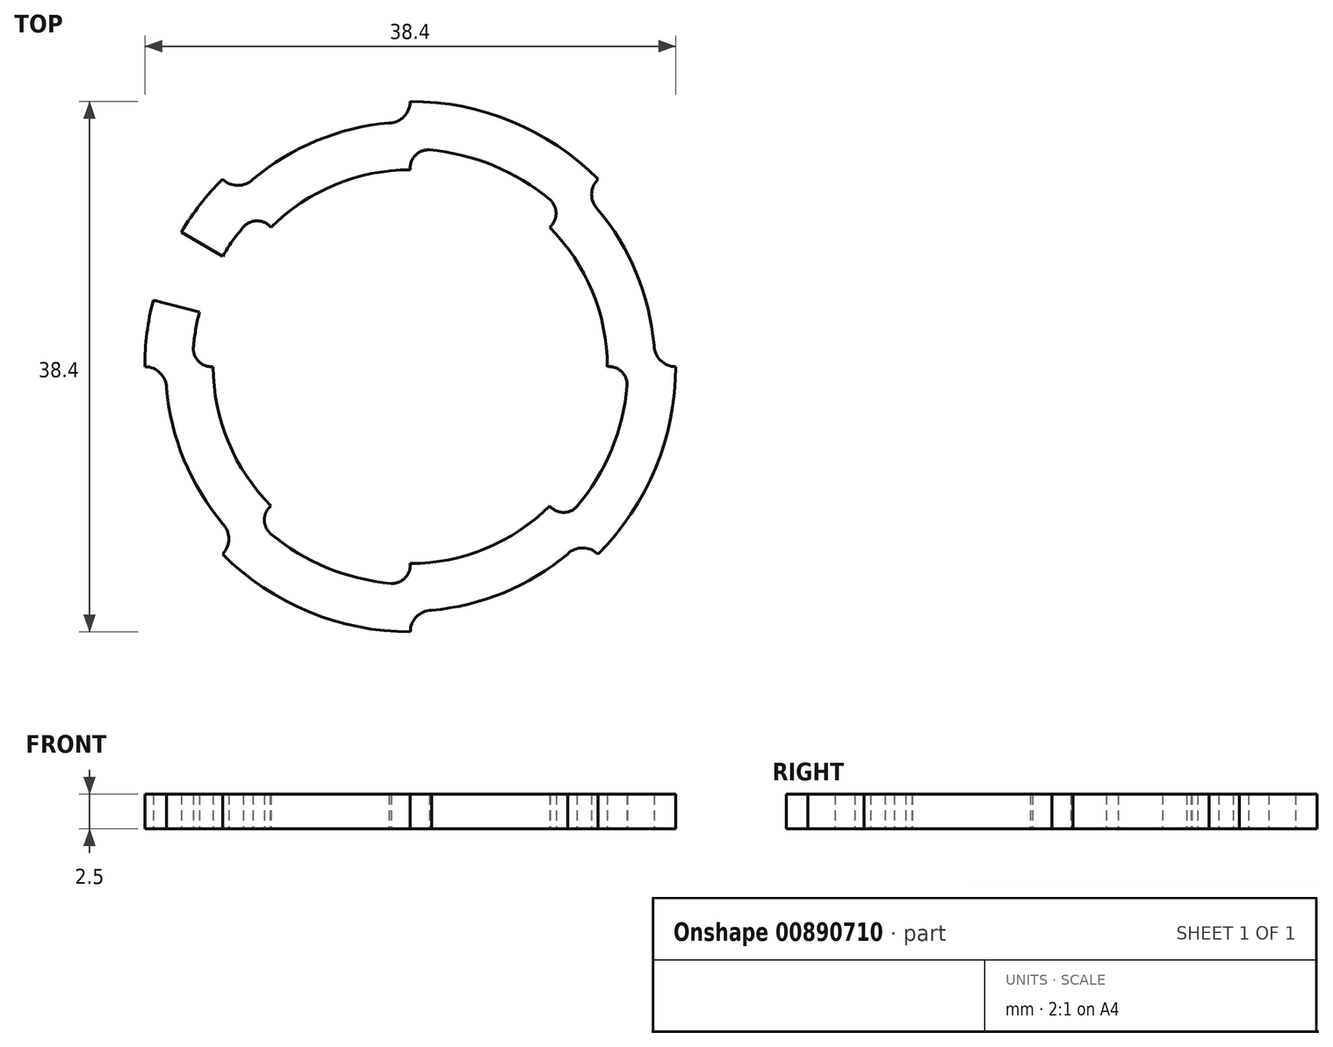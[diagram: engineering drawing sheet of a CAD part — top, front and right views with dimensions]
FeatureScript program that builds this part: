
annotation { "Feature Type Name" : "Feature", "Feature Type Description" : "" }
export const myFeature = defineFeature(function(context is Context, id is Id, definition is map)
    precondition{}
    {
        {
            var Q0;
            Q0=qCreatedBy(makeId("Top.planeOp"),FACE);
            var sketch = newSketch(context, id + "F0", { "sketchPlane" : qUnion([Q0])});
            skCircle(sketch, "E0", {"center": v(0, 0) * mm, "radius": 19.2 * mm, "construction": true});
            skArc(sketch, "E1", {"start": v(-13.58, 13.58) * mm, "mid": v(-17.74, 7.35) * mm, "end": v(-19.2, 0) * mm});
            skArc(sketch, "E2.1.0", {"start": v(13.58, 13.58) * mm, "mid": v(7.35, 17.74) * mm, "end": v(0, 19.2) * mm});
            skArc(sketch, "E2.2.0", {"start": v(13.58, -13.58) * mm, "mid": v(17.74, -7.35) * mm, "end": v(19.2, 0) * mm});
            skArc(sketch, "E2.3.0", {"start": v(-13.58, -13.58) * mm, "mid": v(-7.35, -17.74) * mm, "end": v(0, -19.2) * mm});
            skLineSegment(sketch, "E2.anchor1", {"start": v(0, 0) * mm, "end": v(-19.2, 0) * mm, "construction": true});
            skLineSegment(sketch, "E2.anchor2", {"start": v(0, 0) * mm, "end": v(0, -19.2) * mm, "construction": true});
            skCircle(sketch, "E3", {"center": v(0, 0) * mm, "radius": 17.7 * mm, "construction": true});
            skLineSegment(sketch, "E4", {"start": v(0, 0) * mm, "end": v(13.58, -13.58) * mm, "construction": true});
            skLineSegment(sketch, "E5", {"start": v(0, 0) * mm, "end": v(14.28, -17.02) * mm, "construction": true});
            skLineSegment(sketch, "E6", {"start": v(0, 0) * mm, "end": v(20.43, 1.79) * mm, "construction": true});
            skLineSegment(sketch, "E7", {"start": v(0, 0) * mm, "end": v(1.79, -20.44) * mm, "construction": true});
            skPoint(sketch, "E8", {"position": v(11.38, -13.56) * mm});
            skPoint(sketch, "E9", {"position": v(1.54, -17.63) * mm});
            skPoint(sketch, "E10", {"position": v(17.63, 1.54) * mm});
            skArc(sketch, "E11", {"start": v(13.58, -13.58) * mm, "mid": v(12.48, -13.12) * mm, "end": v(11.38, -13.56) * mm});
            skArc(sketch, "E12", {"start": v(1.54, -17.63) * mm, "mid": v(0.45, -18.1) * mm, "end": v(0, -19.2) * mm});
            skLineSegment(sketch, "E13", {"start": v(0, 0) * mm, "end": v(-20.95, -1.83) * mm, "construction": true});
            skLineSegment(sketch, "E14", {"start": v(0, 0) * mm, "end": v(-13.58, -13.58) * mm, "construction": true});
            skLineSegment(sketch, "E15", {"start": v(0, 0) * mm, "end": v(-18.25, -15.32) * mm, "construction": true});
            skArc(sketch, "E16", {"start": v(17.63, 1.54) * mm, "mid": v(18.1, 0.45) * mm, "end": v(19.2, 0) * mm});
            skArc(sketch, "E17", {"start": v(11.38, -13.56) * mm, "mid": v(6.77, -16.35) * mm, "end": v(1.54, -17.63) * mm});
            skArc(sketch, "E18", {"start": v(-13.56, -11.38) * mm, "mid": v(-16.35, -6.77) * mm, "end": v(-17.63, -1.54) * mm});
            skArc(sketch, "E19", {"start": v(-13.58, -13.58) * mm, "mid": v(-13.12, -12.48) * mm, "end": v(-13.56, -11.38) * mm});
            skArc(sketch, "E20", {"start": v(-17.63, -1.54) * mm, "mid": v(-18.1, -0.45) * mm, "end": v(-19.2, 0) * mm});
            skLineSegment(sketch, "E21", {"start": v(0, 0) * mm, "end": v(-13.58, 13.58) * mm, "construction": true});
            skLineSegment(sketch, "E22", {"start": v(0, 0) * mm, "end": v(-14.48, 17.25) * mm, "construction": true});
            skLineSegment(sketch, "E23", {"start": v(0, 0) * mm, "end": v(-1.93, 22.01) * mm, "construction": true});
            skLineSegment(sketch, "E24", {"start": v(0, 0) * mm, "end": v(13.58, 13.58) * mm, "construction": true});
            skLineSegment(sketch, "E25", {"start": v(0, 0) * mm, "end": v(16.66, 13.98) * mm, "construction": true});
            skArc(sketch, "E26", {"start": v(-11.38, 13.56) * mm, "mid": v(-6.77, 16.35) * mm, "end": v(-1.54, 17.63) * mm});
            skArc(sketch, "E27", {"start": v(13.56, 11.38) * mm, "mid": v(16.35, 6.77) * mm, "end": v(17.63, 1.54) * mm});
            skArc(sketch, "E28", {"start": v(-13.58, 13.58) * mm, "mid": v(-12.48, 13.12) * mm, "end": v(-11.38, 13.56) * mm});
            skArc(sketch, "E29", {"start": v(-1.54, 17.63) * mm, "mid": v(-0.45, 18.1) * mm, "end": v(0, 19.2) * mm});
            skArc(sketch, "E30", {"start": v(13.58, 13.58) * mm, "mid": v(13.12, 12.48) * mm, "end": v(13.56, 11.38) * mm});
            skLineSegment(sketch, "E31", {"start": v(0, 0) * mm, "end": v(17.2, -14.44) * mm, "construction": true});
            skLineSegment(sketch, "E32", {"start": v(0, 0) * mm, "end": v(23.4, -2.05) * mm, "construction": true});
            skArc(sketch, "E33", {"start": v(12.07, -10.12) * mm, "mid": v(14.55, -6.03) * mm, "end": v(15.7, -1.37) * mm});
            skLineSegment(sketch, "E34", {"start": v(0, 0) * mm, "end": v(-1.9, -21.71) * mm, "construction": true});
            skLineSegment(sketch, "E35", {"start": v(0, 0) * mm, "end": v(-14, -16.68) * mm, "construction": true});
            skArc(sketch, "E36", {"start": v(-1.37, -15.7) * mm, "mid": v(-6.03, -14.55) * mm, "end": v(-10.12, -12.07) * mm});
            skLineSegment(sketch, "E37", {"start": v(0, 0) * mm, "end": v(-21.5, 1.88) * mm, "construction": true});
            skLineSegment(sketch, "E38", {"start": v(0, 0) * mm, "end": v(-15.97, 13.4) * mm, "construction": true});
            skLineSegment(sketch, "E39", {"start": v(0, 0) * mm, "end": v(1.9, 21.75) * mm, "construction": true});
            skArc(sketch, "E40", {"start": v(-15.7, 1.37) * mm, "mid": v(-14.55, 6.03) * mm, "end": v(-12.07, 10.12) * mm});
            skLineSegment(sketch, "E41", {"start": v(0, 0) * mm, "end": v(13.2, 15.73) * mm, "construction": true});
            skArc(sketch, "E42", {"start": v(1.37, 15.7) * mm, "mid": v(6.03, 14.55) * mm, "end": v(10.12, 12.07) * mm});
            skPoint(sketch, "E43", {"position": v(-10.08, -10.08) * mm});
            skPoint(sketch, "E44", {"position": v(0, -14.25) * mm});
            skPoint(sketch, "E45", {"position": v(10.08, -10.08) * mm});
            skPoint(sketch, "E46", {"position": v(12.07, -10.12) * mm});
            skPoint(sketch, "E47", {"position": v(10.08, 10.08) * mm});
            skPoint(sketch, "E48", {"position": v(0, 14.25) * mm});
            skPoint(sketch, "E49", {"position": v(14.25, 0) * mm});
            skPoint(sketch, "E50", {"position": v(-10.08, 10.08) * mm});
            skPoint(sketch, "E51", {"position": v(-12.07, 10.12) * mm});
            skPoint(sketch, "E52", {"position": v(1.37, 15.7) * mm});
            skPoint(sketch, "E53", {"position": v(10.12, 12.07) * mm});
            skPoint(sketch, "E54", {"position": v(15.7, -1.37) * mm});
            skPoint(sketch, "E55", {"position": v(-1.37, -15.7) * mm});
            skPoint(sketch, "E56", {"position": v(-10.12, -12.07) * mm});
            skPoint(sketch, "E57", {"position": v(-14.25, 0) * mm});
            skPoint(sketch, "E58", {"position": v(-15.7, 1.37) * mm});
            skArc(sketch, "E59", {"start": v(-10.08, 10.08) * mm, "mid": v(-5.45, 13.17) * mm, "end": v(0, 14.25) * mm});
            skArc(sketch, "E60", {"start": v(10.08, 10.08) * mm, "mid": v(13.17, 5.45) * mm, "end": v(14.25, 0) * mm});
            skArc(sketch, "E61", {"start": v(10.08, -10.08) * mm, "mid": v(5.45, -13.17) * mm, "end": v(0, -14.25) * mm});
            skArc(sketch, "E62", {"start": v(-10.08, -10.08) * mm, "mid": v(-13.17, -5.45) * mm, "end": v(-14.25, 0) * mm});
            skArc(sketch, "E63", {"start": v(-1.37, -15.7) * mm, "mid": v(-0.36, -15.28) * mm, "end": v(0, -14.25) * mm});
            skArc(sketch, "E64", {"start": v(-10.08, -10.08) * mm, "mid": v(-10.55, -11.06) * mm, "end": v(-10.12, -12.07) * mm});
            skArc(sketch, "E65", {"start": v(-15.7, 1.37) * mm, "mid": v(-15.28, 0.36) * mm, "end": v(-14.25, 0) * mm});
            skArc(sketch, "E66", {"start": v(10.08, -10.08) * mm, "mid": v(11.06, -10.55) * mm, "end": v(12.07, -10.12) * mm});
            skArc(sketch, "E67", {"start": v(15.7, -1.37) * mm, "mid": v(15.28, -0.36) * mm, "end": v(14.25, 0) * mm});
            skArc(sketch, "E68", {"start": v(10.08, 10.08) * mm, "mid": v(10.55, 11.06) * mm, "end": v(10.12, 12.07) * mm});
            skArc(sketch, "E69", {"start": v(1.37, 15.7) * mm, "mid": v(0.36, 15.28) * mm, "end": v(0, 14.25) * mm});
            skArc(sketch, "E70", {"start": v(-10.08, 10.08) * mm, "mid": v(-11.06, 10.55) * mm, "end": v(-12.07, 10.12) * mm});
            skSolve(sketch);
        }
        {
            var Q0;
            Q0=makeQuery(id+"F0.imprint","IMPRINT",FACE,{"disambiguationData":[TD([[makeQuery(id+"F0.imprint","IMPRINT",EDGE,{"derivedFrom":sQuery(id+"F0.wireOp",EDGE,"E1")}),1.0]])]});
            extrude(context, id + "F1", {"entities" : qUnion([Q0]), "depth" : 2.5 * mm, "offsetDistance" : 25 * mm});
        }
        {
            var Q0;
            Q0=qCreatedBy(makeId("Top.planeOp"),FACE);
            var sketch = newSketch(context, id + "F2", { "sketchPlane" : qUnion([Q0])});
            skLineSegment(sketch, "E71", {"start": v(0, 0) * mm, "end": v(-27.93, 11.57) * mm, "construction": true});
            skLineSegment(sketch, "E72", {"start": v(0, 0) * mm, "end": v(-25.86, 15.23) * mm, "construction": true});
            skLineSegment(sketch, "E73", {"start": v(0, 0) * mm, "end": v(-29, 7.5) * mm, "construction": true});
            skArc(sketch, "E74.0", {"start": v(-15.7, 1.37) * mm, "mid": v(-14.55, 6.03) * mm, "end": v(-12.07, 10.12) * mm});
            skArc(sketch, "E75.0", {"start": v(-13.58, 13.58) * mm, "mid": v(-17.74, 7.35) * mm, "end": v(-19.2, 0) * mm});
            skPoint(sketch, "E76", {"position": v(-16.54, 9.74) * mm});
            skPoint(sketch, "E77", {"position": v(-13.57, 8) * mm});
            skPoint(sketch, "E78", {"position": v(-15.25, 3.94) * mm});
            skPoint(sketch, "E79", {"position": v(-18.59, 4.8) * mm});
            skArc(sketch, "E80", {"start": v(-15.25, 3.94) * mm, "mid": v(-14.55, 6.03) * mm, "end": v(-13.57, 8) * mm});
            skLineSegment(sketch, "E81", {"start": v(-15.25, 3.94) * mm, "end": v(-18.59, 4.8) * mm});
            skLineSegment(sketch, "E82", {"start": v(-16.54, 9.74) * mm, "end": v(-13.57, 8) * mm});
            skSolve(sketch);
        }
        {
            var Q0;
            {var subQ0=sQuery(id+"F2.wireOp",EDGE,"E81");Q0=makeQuery(id+"F2.imprint","IMPRINT",FACE,{"disambiguationData":[TD([[makeQuery(id+"F2.imprint","IMPRINT",EDGE,{"derivedFrom":subQ0}),-1.0]])]});}
            extrude(context, id + "F3", {"entities" : qUnion([Q0]), "operationType" : NewBodyOperationType.REMOVE, "endBound" : BoundingType.THROUGH_ALL, "depth" : 25 * mm, "offsetDistance" : 25 * mm});
        }
    });
